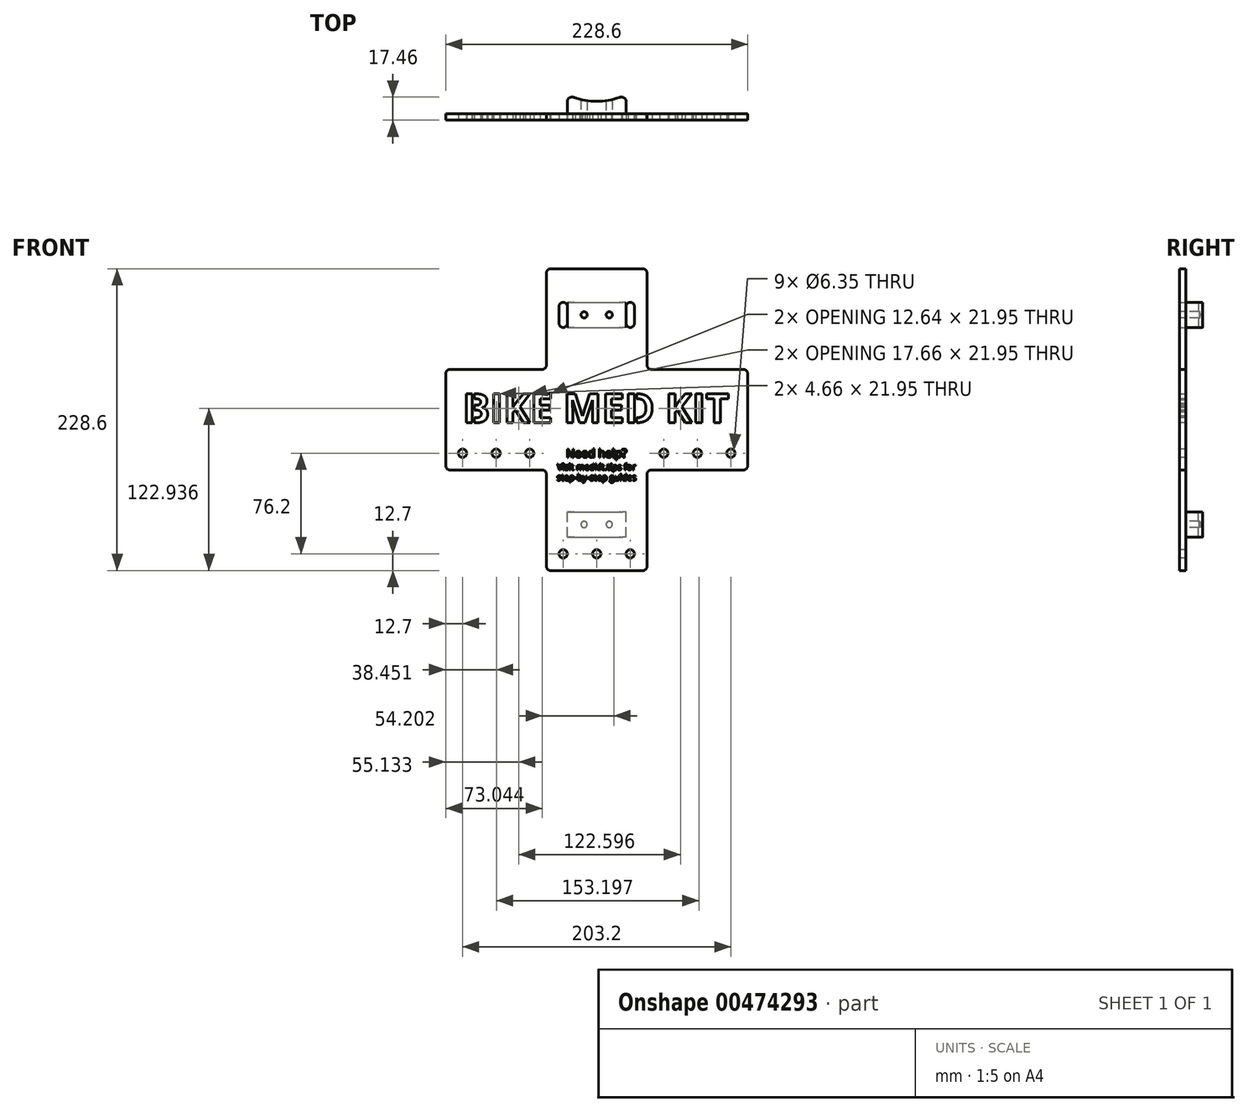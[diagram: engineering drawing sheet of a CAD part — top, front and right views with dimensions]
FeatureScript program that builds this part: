
annotation { "Feature Type Name" : "Feature", "Feature Type Description" : "" }
export const myFeature = defineFeature(function(context is Context, id is Id, definition is map)
    precondition{}
    {
        {
            var Q0;
            Q0=qCreatedBy(makeId("Front.planeOp"),FACE);
            var sketch = newSketch(context, id + "F0", { "sketchPlane" : qUnion([Q0])});
            skLineSegment(sketch, "E0.bottom", {"start": v(-38.1, 114.3) * mm, "end": v(38.1, 114.3) * mm});
            skLineSegment(sketch, "E0.top", {"start": v(-38.1, -114.3) * mm, "end": v(38.1, -114.3) * mm});
            skLineSegment(sketch, "E0.left", {"start": v(-38.1, 114.3) * mm, "end": v(-38.1, 38.1) * mm});
            skLineSegment(sketch, "E0.right", {"start": v(38.1, 114.3) * mm, "end": v(38.1, 38.1) * mm});
            skPoint(sketch, "E0.middle", {"position": v(0, 0) * mm});
            skLineSegment(sketch, "E1.bottom", {"start": v(114.3, 38.1) * mm, "end": v(38.1, 38.1) * mm});
            skLineSegment(sketch, "E1.top", {"start": v(114.3, -38.1) * mm, "end": v(38.1, -38.1) * mm});
            skLineSegment(sketch, "E1.left", {"start": v(114.3, 38.1) * mm, "end": v(114.3, -38.1) * mm});
            skLineSegment(sketch, "E1.right", {"start": v(-114.3, 38.1) * mm, "end": v(-114.3, -38.1) * mm});
            skLineSegment(sketch, "E2.trimOffspring", {"start": v(-38.1, 38.1) * mm, "end": v(-114.3, 38.1) * mm});
            skLineSegment(sketch, "E3.trimOffspring", {"start": v(-38.1, -38.1) * mm, "end": v(-38.1, -114.3) * mm});
            skLineSegment(sketch, "E4.trimOffspring", {"start": v(-38.1, -38.1) * mm, "end": v(-114.3, -38.1) * mm});
            skLineSegment(sketch, "E5.trimOffspring", {"start": v(38.1, -38.1) * mm, "end": v(38.1, -114.3) * mm});
            skSolve(sketch);
        }
        {
            var Q0;
            Q0 = qSketchRegion(id + "F0", true);
            extrude(context, id + "F1", {"entities" : qUnion([Q0]), "oppositeDirection" : true, "depth" : 4.76 * mm});
        }
        {
            var Q0;
            Q0=makeQuery(id+"F1.opExtrude","SWEPT_EDGE",EDGE,{"disambiguationData":[OSD([sQuery(id+"F0.wireOp",EDGE,"E0.right"),sQuery(id+"F0.wireOp",EDGE,"E1.bottom")])]});
            var Q1;
            Q1=makeQuery(id+"F1.opExtrude","SWEPT_EDGE",EDGE,{"disambiguationData":[OSD([sQuery(id+"F0.wireOp",EDGE,"E1.bottom"),sQuery(id+"F0.wireOp",EDGE,"E1.left")])]});
            var Q2;
            Q2=makeQuery(id+"F1.opExtrude","SWEPT_EDGE",EDGE,{"disambiguationData":[OSD([sQuery(id+"F0.wireOp",EDGE,"E1.top"),sQuery(id+"F0.wireOp",EDGE,"E1.left")])]});
            var Q3;
            Q3=makeQuery(id+"F1.opExtrude","SWEPT_EDGE",EDGE,{"disambiguationData":[OSD([sQuery(id+"F0.wireOp",EDGE,"E1.right"),sQuery(id+"F0.wireOp",EDGE,"E2.trimOffspring")])]});
            var Q4;
            Q4=makeQuery(id+"F1.opExtrude","SWEPT_EDGE",EDGE,{"disambiguationData":[OSD([sQuery(id+"F0.wireOp",EDGE,"E1.right"),sQuery(id+"F0.wireOp",EDGE,"E4.trimOffspring")])]});
            var Q5;
            Q5=makeQuery(id+"F1.opExtrude","SWEPT_EDGE",EDGE,{"disambiguationData":[OSD([sQuery(id+"F0.wireOp",EDGE,"E3.trimOffspring"),sQuery(id+"F0.wireOp",EDGE,"E4.trimOffspring")])]});
            var Q6;
            Q6=makeQuery(id+"F1.opExtrude","SWEPT_EDGE",EDGE,{"disambiguationData":[OSD([sQuery(id+"F0.wireOp",EDGE,"E1.top"),sQuery(id+"F0.wireOp",EDGE,"E5.trimOffspring")])]});
            var Q7;
            Q7=makeQuery(id+"F1.opExtrude","SWEPT_EDGE",EDGE,{"disambiguationData":[OSD([sQuery(id+"F0.wireOp",EDGE,"E0.left"),sQuery(id+"F0.wireOp",EDGE,"E2.trimOffspring")])]});
            var Q8;
            Q8=makeQuery(id+"F1.opExtrude","SWEPT_EDGE",EDGE,{"disambiguationData":[OSD([sQuery(id+"F0.wireOp",EDGE,"E0.bottom"),sQuery(id+"F0.wireOp",EDGE,"E0.right")])]});
            var Q9;
            Q9=makeQuery(id+"F1.opExtrude","SWEPT_EDGE",EDGE,{"disambiguationData":[OSD([sQuery(id+"F0.wireOp",EDGE,"E0.bottom"),sQuery(id+"F0.wireOp",EDGE,"E0.left")])]});
            var Q10;
            Q10=makeQuery(id+"F1.opExtrude","SWEPT_EDGE",EDGE,{"disambiguationData":[OSD([sQuery(id+"F0.wireOp",EDGE,"E0.top"),sQuery(id+"F0.wireOp",EDGE,"E5.trimOffspring")])]});
            var Q11;
            Q11=makeQuery(id+"F1.opExtrude","SWEPT_EDGE",EDGE,{"disambiguationData":[OSD([sQuery(id+"F0.wireOp",EDGE,"E0.top"),sQuery(id+"F0.wireOp",EDGE,"E3.trimOffspring")])]});
            fillet(context, id + "F2", {"entities" : qUnion([Q0, Q1, Q2, Q3, Q4, Q5, Q6, Q7, Q8, Q9, Q10, Q11]), "radius" : 3.17 * mm, "tangentPropagation" : true, "allowEdgeOverflow" : false});
        }
        {
            var Q0;
            Q0=makeQuery(id+"F1.opExtrude","CAP_FACE",FACE,{"disambiguationData":[OSD([sQuery(id+"F0.wireOp",EDGE,"E0.bottom"),sQuery(id+"F0.wireOp",EDGE,"E0.top"),sQuery(id+"F0.wireOp",EDGE,"E0.left"),sQuery(id+"F0.wireOp",EDGE,"E0.right"),sQuery(id+"F0.wireOp",EDGE,"E1.bottom"),sQuery(id+"F0.wireOp",EDGE,"E1.top"),sQuery(id+"F0.wireOp",EDGE,"E1.left"),sQuery(id+"F0.wireOp",EDGE,"E1.right"),sQuery(id+"F0.wireOp",EDGE,"E2.trimOffspring"),sQuery(id+"F0.wireOp",EDGE,"E3.trimOffspring"),sQuery(id+"F0.wireOp",EDGE,"E4.trimOffspring"),sQuery(id+"F0.wireOp",EDGE,"E5.trimOffspring")])],"isStart":true});
            var sketch = newSketch(context, id + "F3", { "sketchPlane" : qUnion([Q0])});
            skCircle(sketch, "E6", {"center": v(-101.6, -25.4) * mm, "radius": 3.18 * mm});
            skCircle(sketch, "E7.1.0.0", {"center": v(-76.2, -25.4) * mm, "radius": 3.18 * mm});
            skCircle(sketch, "E7.2.0.0", {"center": v(-50.8, -25.4) * mm, "radius": 3.18 * mm});
            skLineSegment(sketch, "E7.direction1", {"start": v(-101.6, -25.4) * mm, "end": v(-76.2, -25.4) * mm, "construction": true});
            skCircle(sketch, "E8", {"center": v(-25.4, -101.6) * mm, "radius": 3.18 * mm});
            skCircle(sketch, "E9", {"center": v(101.6, -25.4) * mm, "radius": 3.18 * mm});
            skCircle(sketch, "E10.1.0.0", {"center": v(76.2, -25.4) * mm, "radius": 3.18 * mm});
            skCircle(sketch, "E10.2.0.0", {"center": v(50.8, -25.4) * mm, "radius": 3.18 * mm});
            skLineSegment(sketch, "E10.direction1", {"start": v(101.6, -25.4) * mm, "end": v(76.2, -25.4) * mm, "construction": true});
            skCircle(sketch, "E11.1.0.0", {"center": v(0, -101.6) * mm, "radius": 3.18 * mm});
            skCircle(sketch, "E11.2.0.0", {"center": v(25.4, -101.6) * mm, "radius": 3.18 * mm});
            skLineSegment(sketch, "E11.direction1", {"start": v(-25.4, -101.6) * mm, "end": v(0, -101.6) * mm, "construction": true});
            skSolve(sketch);
        }
        {
            var Q0;
            Q0 = qSketchRegion(id + "F3", true);
            extrude(context, id + "F4", {"entities" : qUnion([Q0]), "operationType" : NewBodyOperationType.REMOVE, "endBound" : BoundingType.THROUGH_ALL, "oppositeDirection" : true, "depth" : 25.4 * mm});
        }
        {
            var Q0;
            Q0=makeQuery(id+"F1.opExtrude","CAP_FACE",FACE,{"disambiguationData":[OSD([sQuery(id+"F0.wireOp",EDGE,"E0.bottom"),sQuery(id+"F0.wireOp",EDGE,"E0.top"),sQuery(id+"F0.wireOp",EDGE,"E0.left"),sQuery(id+"F0.wireOp",EDGE,"E0.right"),sQuery(id+"F0.wireOp",EDGE,"E1.bottom"),sQuery(id+"F0.wireOp",EDGE,"E1.top"),sQuery(id+"F0.wireOp",EDGE,"E1.left"),sQuery(id+"F0.wireOp",EDGE,"E1.right"),sQuery(id+"F0.wireOp",EDGE,"E2.trimOffspring"),sQuery(id+"F0.wireOp",EDGE,"E3.trimOffspring"),sQuery(id+"F0.wireOp",EDGE,"E4.trimOffspring"),sQuery(id+"F0.wireOp",EDGE,"E5.trimOffspring")])],"isStart":true});
            var sketch = newSketch(context, id + "F5", { "sketchPlane" : qUnion([Q0])});
            skText(sketch, "E12", { "text": "BIKE MED KIT", "fontName": "OpenSans-Bold.ttf"});
            skLineSegment(sketch, "E13", {"start": v(-101.6, -22.23) * mm, "end": v(-50.8, -22.22) * mm, "construction": true});
            skLineSegment(sketch, "E14", {"start": v(-101.6, 7.94) * mm, "end": v(101.6, 7.94) * mm, "construction": true});
            const initialGuessF5  = {"E12": [-0.1016, -0.00234, 1, 0, 0.02214]};
            skSetInitialGuess(sketch, initialGuessF5);
            skSolve(sketch);
        }
        {
            var Q0;
            Q0 = qSketchRegion(id + "F5", true);
            extrude(context, id + "F6", {"entities" : qUnion([Q0]), "operationType" : NewBodyOperationType.REMOVE, "endBound" : BoundingType.THROUGH_ALL, "oppositeDirection" : true, "depth" : 25.4 * mm});
        }
        {
            var Q0;
            {var subQ0=sQuery(id+"F0.wireOp",EDGE,"E2.trimOffspring");var subQ1=sQuery(id+"F0.wireOp",EDGE,"E1.right");var subQ2=sQuery(id+"F0.wireOp",EDGE,"E5.trimOffspring");var subQ3=sQuery(id+"F0.wireOp",EDGE,"E1.top");var subQ4=sQuery(id+"F0.wireOp",EDGE,"E1.left");var subQ5=sQuery(id+"F0.wireOp",EDGE,"E0.left");var subQ6=sQuery(id+"F0.wireOp",EDGE,"E1.bottom");var subQ7=sQuery(id+"F0.wireOp",EDGE,"E4.trimOffspring");var subQ8=sQuery(id+"F0.wireOp",EDGE,"E0.top");var subQ9=sQuery(id+"F0.wireOp",EDGE,"E0.right");var subQ10=sQuery(id+"F0.wireOp",EDGE,"E0.bottom");var subQ11=sQuery(id+"F0.wireOp",EDGE,"E3.trimOffspring");Q0=makeQuery(id+"F6.boolean.opBoolean","SPLIT",FACE,{"disambiguationData":[TD([makeQuery(id+"F1.opExtrude","SWEPT_FACE",FACE,{"disambiguationData":[OSD([subQ10])]})])],"derivedFrom":makeQuery(id+"F1.opExtrude","CAP_FACE",FACE,{"disambiguationData":[OSD([subQ10,subQ8,subQ5,subQ9,subQ6,subQ3,subQ4,subQ1,subQ0,subQ11,subQ7,subQ2])],"isStart":true})});}
            var sketch = newSketch(context, id + "F7", { "sketchPlane" : qUnion([Q0])});
            skLineSegment(sketch, "E15.bottom", {"start": v(-94.18, 23) * mm, "end": v(-92.6, 23) * mm});
            skLineSegment(sketch, "E15.top", {"start": v(-94.18, -7.38) * mm, "end": v(-92.6, -7.38) * mm});
            skLineSegment(sketch, "E15.left", {"start": v(-94.18, 23) * mm, "end": v(-94.18, -7.38) * mm});
            skLineSegment(sketch, "E15.right", {"start": v(-92.6, 23) * mm, "end": v(-92.6, -7.38) * mm});
            skLineSegment(sketch, "E16.bottom", {"start": v(28.49, 25.23) * mm, "end": v(30.07, 25.23) * mm});
            skLineSegment(sketch, "E16.top", {"start": v(28.49, -11.56) * mm, "end": v(30.07, -11.56) * mm});
            skLineSegment(sketch, "E16.left", {"start": v(28.49, 25.23) * mm, "end": v(28.49, -11.56) * mm});
            skLineSegment(sketch, "E16.right", {"start": v(30.07, 25.23) * mm, "end": v(30.07, -11.56) * mm});
            skSolve(sketch);
        }
        {
            var Q0;
            Q0 = qSketchRegion(id + "F7", true);
            var Q1;
            {var subQ0=sQuery(id+"F0.wireOp",EDGE,"E2.trimOffspring");var subQ1=sQuery(id+"F0.wireOp",EDGE,"E1.right");var subQ2=sQuery(id+"F0.wireOp",EDGE,"E5.trimOffspring");var subQ3=sQuery(id+"F0.wireOp",EDGE,"E1.top");var subQ4=sQuery(id+"F0.wireOp",EDGE,"E1.left");var subQ5=sQuery(id+"F0.wireOp",EDGE,"E0.left");var subQ6=sQuery(id+"F0.wireOp",EDGE,"E1.bottom");var subQ7=sQuery(id+"F0.wireOp",EDGE,"E4.trimOffspring");var subQ8=sQuery(id+"F0.wireOp",EDGE,"E0.top");var subQ9=sQuery(id+"F0.wireOp",EDGE,"E0.right");var subQ10=sQuery(id+"F0.wireOp",EDGE,"E0.bottom");var subQ11=sQuery(id+"F0.wireOp",EDGE,"E3.trimOffspring");Q1=makeQuery(id+"F6.boolean.opBoolean","SPLIT",FACE,{"disambiguationData":[TD([makeQuery(id+"F1.opExtrude","SWEPT_FACE",FACE,{"disambiguationData":[OSD([subQ10])]})])],"derivedFrom":makeQuery(id+"F1.opExtrude","CAP_FACE",FACE,{"disambiguationData":[OSD([subQ10,subQ8,subQ5,subQ9,subQ6,subQ3,subQ4,subQ1,subQ0,subQ11,subQ7,subQ2])],"isStart":false})});}
            extrude(context, id + "F8", {"entities" : qUnion([Q0]), "operationType" : NewBodyOperationType.ADD, "endBound" : BoundingType.UP_TO_SURFACE, "oppositeDirection" : true, "endBoundEntityFace" : qUnion([Q1]), "depth" : 25.4 * mm});
        }
        {
            var Q0;
            {var subQ0=sQuery(id+"F0.wireOp",EDGE,"E5.trimOffspring");var subQ1=sQuery(id+"F0.wireOp",EDGE,"E4.trimOffspring");var subQ2=sQuery(id+"F0.wireOp",EDGE,"E3.trimOffspring");var subQ3=sQuery(id+"F0.wireOp",EDGE,"E2.trimOffspring");var subQ4=sQuery(id+"F0.wireOp",EDGE,"E1.right");var subQ5=sQuery(id+"F0.wireOp",EDGE,"E1.left");var subQ6=sQuery(id+"F0.wireOp",EDGE,"E1.top");var subQ7=sQuery(id+"F0.wireOp",EDGE,"E1.bottom");var subQ8=sQuery(id+"F0.wireOp",EDGE,"E0.right");var subQ9=sQuery(id+"F0.wireOp",EDGE,"E0.left");var subQ10=sQuery(id+"F0.wireOp",EDGE,"E0.top");var subQ11=sQuery(id+"F0.wireOp",EDGE,"E0.bottom");var subQ12=makeQuery(id+"F1.opExtrude","CAP_FACE",FACE,{"disambiguationData":[OSD([subQ11,subQ10,subQ9,subQ8,subQ7,subQ6,subQ5,subQ4,subQ3,subQ2,subQ1,subQ0])],"isStart":true});Q0=makeQuery(id+"F8.boolean.opBoolean","MERGE",FACE,{"derivedFrom":[makeQuery(id+"F6.boolean.opBoolean","SPLIT",FACE,{"disambiguationData":[TD([makeQuery(id+"F1.opExtrude","SWEPT_FACE",FACE,{"disambiguationData":[OSD([subQ11])]})])],"derivedFrom":subQ12}),makeQuery(id+"F6.boolean.opBoolean","SPLIT",FACE,{"disambiguationData":[TD([makeQuery(id+"F6.opExtrude","SWEPT_FACE",FACE,{"disambiguationData":[OSD([sQuery(id+"F5.wireOp",EDGE,"E12.sketch_text.stroke-12")])]})])],"derivedFrom":subQ12}),makeQuery(id+"F6.boolean.opBoolean","SPLIT",FACE,{"disambiguationData":[TD([makeQuery(id+"F6.opExtrude","SWEPT_FACE",FACE,{"disambiguationData":[OSD([sQuery(id+"F5.wireOp",EDGE,"E12.sketch_text.stroke-19")])]})])],"derivedFrom":subQ12}),makeQuery(id+"F6.boolean.opBoolean","SPLIT",FACE,{"disambiguationData":[TD([makeQuery(id+"F6.opExtrude","SWEPT_FACE",FACE,{"disambiguationData":[OSD([sQuery(id+"F5.wireOp",EDGE,"E12.sketch_text.stroke-92")])]})])],"derivedFrom":subQ12}),makeQuery(id+"F8.opExtrude","CAP_FACE",FACE,{"disambiguationData":[OSD([sQuery(id+"F7.wireOp",EDGE,"E15.bottom"),sQuery(id+"F7.wireOp",EDGE,"E15.top"),sQuery(id+"F7.wireOp",EDGE,"E15.left"),sQuery(id+"F7.wireOp",EDGE,"E15.right")])],"isStart":true}),makeQuery(id+"F8.opExtrude","CAP_FACE",FACE,{"disambiguationData":[OSD([sQuery(id+"F7.wireOp",EDGE,"E16.bottom"),sQuery(id+"F7.wireOp",EDGE,"E16.top"),sQuery(id+"F7.wireOp",EDGE,"E16.left"),sQuery(id+"F7.wireOp",EDGE,"E16.right")])],"isStart":true})]});}
            var sketch = newSketch(context, id + "F9", { "sketchPlane" : qUnion([Q0])});
            skLineSegment(sketch, "E17.bottom", {"start": v(-28.57, 88.9) * mm, "end": v(-22.22, 88.9) * mm});
            skLineSegment(sketch, "E17.top", {"start": v(-28.57, 69.85) * mm, "end": v(-22.22, 69.85) * mm});
            skLineSegment(sketch, "E17.left", {"start": v(-28.57, 88.9) * mm, "end": v(-28.57, 69.85) * mm});
            skLineSegment(sketch, "E17.right", {"start": v(-22.22, 88.9) * mm, "end": v(-22.22, 69.85) * mm});
            skLineSegment(sketch, "E18.MirrorCS", {"start": v(22.22, 88.9) * mm, "end": v(22.22, 69.85) * mm});
            skLineSegment(sketch, "E19.MirrorCS", {"start": v(28.57, 69.85) * mm, "end": v(22.22, 69.85) * mm});
            skLineSegment(sketch, "E20.MirrorCS", {"start": v(28.57, 88.9) * mm, "end": v(28.57, 69.85) * mm});
            skLineSegment(sketch, "E21.MirrorCS", {"start": v(28.57, 88.9) * mm, "end": v(22.22, 88.9) * mm});
            skSolve(sketch);
        }
        {
            var Q0;
            Q0 = qSketchRegion(id + "F9", true);
            extrude(context, id + "F10", {"entities" : qUnion([Q0]), "operationType" : NewBodyOperationType.REMOVE, "endBound" : BoundingType.THROUGH_ALL, "oppositeDirection" : true, "depth" : 25.4 * mm});
        }
        {
            var Q0;
            Q0=makeQuery(id+"F10.boolean.opBoolean","COPY",EDGE,{"derivedFrom":makeQuery(id+"F10.opExtrude","SWEPT_EDGE",EDGE,{"disambiguationData":[OSD([sQuery(id+"F9.wireOp",EDGE,"E17.top"),sQuery(id+"F9.wireOp",EDGE,"E17.left")])]})});
            var Q1;
            Q1=makeQuery(id+"F10.boolean.opBoolean","COPY",EDGE,{"derivedFrom":makeQuery(id+"F10.opExtrude","SWEPT_EDGE",EDGE,{"disambiguationData":[OSD([sQuery(id+"F9.wireOp",EDGE,"E17.top"),sQuery(id+"F9.wireOp",EDGE,"E17.right")])]})});
            var Q2;
            Q2=makeQuery(id+"F10.boolean.opBoolean","COPY",EDGE,{"derivedFrom":makeQuery(id+"F10.opExtrude","SWEPT_EDGE",EDGE,{"disambiguationData":[OSD([sQuery(id+"F9.wireOp",EDGE,"E19.MirrorCS"),sQuery(id+"F9.wireOp",EDGE,"E20.MirrorCS")])]})});
            var Q3;
            Q3=makeQuery(id+"F10.boolean.opBoolean","COPY",EDGE,{"derivedFrom":makeQuery(id+"F10.opExtrude","SWEPT_EDGE",EDGE,{"disambiguationData":[OSD([sQuery(id+"F9.wireOp",EDGE,"E18.MirrorCS"),sQuery(id+"F9.wireOp",EDGE,"E19.MirrorCS")])]})});
            var Q4;
            Q4=makeQuery(id+"F10.boolean.opBoolean","COPY",EDGE,{"derivedFrom":makeQuery(id+"F10.opExtrude","SWEPT_EDGE",EDGE,{"disambiguationData":[OSD([sQuery(id+"F9.wireOp",EDGE,"E18.MirrorCS"),sQuery(id+"F9.wireOp",EDGE,"E21.MirrorCS")])]})});
            var Q5;
            Q5=makeQuery(id+"F10.boolean.opBoolean","COPY",EDGE,{"derivedFrom":makeQuery(id+"F10.opExtrude","SWEPT_EDGE",EDGE,{"disambiguationData":[OSD([sQuery(id+"F9.wireOp",EDGE,"E17.bottom"),sQuery(id+"F9.wireOp",EDGE,"E17.left")])]})});
            var Q6;
            Q6=makeQuery(id+"F10.boolean.opBoolean","COPY",EDGE,{"derivedFrom":makeQuery(id+"F10.opExtrude","SWEPT_EDGE",EDGE,{"disambiguationData":[OSD([sQuery(id+"F9.wireOp",EDGE,"E17.bottom"),sQuery(id+"F9.wireOp",EDGE,"E17.right")])]})});
            var Q7;
            Q7=makeQuery(id+"F10.boolean.opBoolean","COPY",EDGE,{"derivedFrom":makeQuery(id+"F10.opExtrude","SWEPT_EDGE",EDGE,{"disambiguationData":[OSD([sQuery(id+"F9.wireOp",EDGE,"E20.MirrorCS"),sQuery(id+"F9.wireOp",EDGE,"E21.MirrorCS")])]})});
            fillet(context, id + "F11", {"entities" : qUnion([Q0, Q1, Q2, Q3, Q4, Q5, Q6, Q7]), "radius" : 3.17 * mm, "tangentPropagation" : true, "allowEdgeOverflow" : false});
        }
        {
            var Q0;
            {var subQ0=sQuery(id+"F0.wireOp",EDGE,"E5.trimOffspring");var subQ1=sQuery(id+"F0.wireOp",EDGE,"E4.trimOffspring");var subQ2=sQuery(id+"F0.wireOp",EDGE,"E3.trimOffspring");var subQ3=sQuery(id+"F0.wireOp",EDGE,"E2.trimOffspring");var subQ4=sQuery(id+"F0.wireOp",EDGE,"E1.right");var subQ5=sQuery(id+"F0.wireOp",EDGE,"E1.left");var subQ6=sQuery(id+"F0.wireOp",EDGE,"E1.top");var subQ7=sQuery(id+"F0.wireOp",EDGE,"E1.bottom");var subQ8=sQuery(id+"F0.wireOp",EDGE,"E0.right");var subQ9=sQuery(id+"F0.wireOp",EDGE,"E0.left");var subQ10=sQuery(id+"F0.wireOp",EDGE,"E0.top");var subQ11=sQuery(id+"F0.wireOp",EDGE,"E0.bottom");var subQ12=makeQuery(id+"F1.opExtrude","CAP_FACE",FACE,{"disambiguationData":[OSD([subQ11,subQ10,subQ9,subQ8,subQ7,subQ6,subQ5,subQ4,subQ3,subQ2,subQ1,subQ0])],"isStart":true});Q0=makeQuery(id+"F8.boolean.opBoolean","MERGE",FACE,{"derivedFrom":[makeQuery(id+"F6.boolean.opBoolean","SPLIT",FACE,{"disambiguationData":[TD([makeQuery(id+"F1.opExtrude","SWEPT_FACE",FACE,{"disambiguationData":[OSD([subQ11])]})])],"derivedFrom":subQ12}),makeQuery(id+"F6.boolean.opBoolean","SPLIT",FACE,{"disambiguationData":[TD([makeQuery(id+"F6.opExtrude","SWEPT_FACE",FACE,{"disambiguationData":[OSD([sQuery(id+"F5.wireOp",EDGE,"E12.sketch_text.stroke-12")])]})])],"derivedFrom":subQ12}),makeQuery(id+"F6.boolean.opBoolean","SPLIT",FACE,{"disambiguationData":[TD([makeQuery(id+"F6.opExtrude","SWEPT_FACE",FACE,{"disambiguationData":[OSD([sQuery(id+"F5.wireOp",EDGE,"E12.sketch_text.stroke-19")])]})])],"derivedFrom":subQ12}),makeQuery(id+"F6.boolean.opBoolean","SPLIT",FACE,{"disambiguationData":[TD([makeQuery(id+"F6.opExtrude","SWEPT_FACE",FACE,{"disambiguationData":[OSD([sQuery(id+"F5.wireOp",EDGE,"E12.sketch_text.stroke-92")])]})])],"derivedFrom":subQ12}),makeQuery(id+"F8.opExtrude","CAP_FACE",FACE,{"disambiguationData":[OSD([sQuery(id+"F7.wireOp",EDGE,"E15.bottom"),sQuery(id+"F7.wireOp",EDGE,"E15.top"),sQuery(id+"F7.wireOp",EDGE,"E15.left"),sQuery(id+"F7.wireOp",EDGE,"E15.right")])],"isStart":true}),makeQuery(id+"F8.opExtrude","CAP_FACE",FACE,{"disambiguationData":[OSD([sQuery(id+"F7.wireOp",EDGE,"E16.bottom"),sQuery(id+"F7.wireOp",EDGE,"E16.top"),sQuery(id+"F7.wireOp",EDGE,"E16.left"),sQuery(id+"F7.wireOp",EDGE,"E16.right")])],"isStart":true})]});}
            var sketch = newSketch(context, id + "F12", { "sketchPlane" : qUnion([Q0])});
            skCircle(sketch, "E22", {"center": v(-9.53, 79.38) * mm, "radius": 2.38 * mm});
            skCircle(sketch, "E23", {"center": v(9.53, 79.38) * mm, "radius": 2.38 * mm});
            skLineSegment(sketch, "E24", {"start": v(-22.22, 79.38) * mm, "end": v(22.22, 79.38) * mm, "construction": true});
            skSolve(sketch);
        }
        {
            var Q0;
            Q0 = qSketchRegion(id + "F12", true);
            extrude(context, id + "F13", {"entities" : qUnion([Q0]), "operationType" : NewBodyOperationType.REMOVE, "endBound" : BoundingType.THROUGH_ALL, "oppositeDirection" : true, "depth" : 25.4 * mm});
        }
        {
            var Q0;
            Q0=qCreatedBy(makeId("Top.planeOp"),FACE);
            cPlane(context, id + "F14", {"entities" : qUnion([Q0]), "cplaneType" : CPlaneType.OFFSET, "offset" : 79.38 * mm, "width" : 152.4 * mm, "height" : 152.4 * mm});
        }
        {
            var Q0;
            Q0=qCreatedBy(id+"F14.planeOp",FACE);
            var sketch = newSketch(context, id + "F15", { "sketchPlane" : qUnion([Q0])});
            skLineSegment(sketch, "E25.bottom", {"start": v(-22.22, 4.76) * mm, "end": v(22.23, 4.76) * mm});
            skLineSegment(sketch, "E25.top", {"start": v(-22.22, 17.46) * mm, "end": v(-17.68, 17.46) * mm});
            skLineSegment(sketch, "E25.left", {"start": v(-22.22, 4.76) * mm, "end": v(-22.22, 17.46) * mm});
            skLineSegment(sketch, "E25.right", {"start": v(22.23, 4.76) * mm, "end": v(22.23, 17.46) * mm});
            skArc(sketch, "E26", {"start": v(-17.68, 17.46) * mm, "mid": v(0, 14.29) * mm, "end": v(17.68, 17.46) * mm});
            skLineSegment(sketch, "E27", {"start": v(0, 17.46) * mm, "end": v(0, 65.09) * mm, "construction": true});
            skPoint(sketch, "E27.endSnap0", {"position": v(0, 17.46) * mm});
            skLineSegment(sketch, "E28.trimOffspring", {"start": v(17.68, 17.46) * mm, "end": v(22.23, 17.46) * mm});
            skSolve(sketch);
        }
        {
            var Q0;
            Q0 = qSketchRegion(id + "F15", true);
            extrude(context, id + "F16", {"entities" : qUnion([Q0]), "depth" : 9.52 * mm, "hasSecondDirection" : true, "secondDirectionOppositeDirection" : true, "secondDirectionDepth" : 9.52 * mm});
        }
        {
            var Q0;
            Q0=makeQuery(id+"F16.opExtrude","SWEPT_EDGE",EDGE,{"disambiguationData":[OSD([sQuery(id+"F15.wireOp",EDGE,"E26"),sQuery(id+"F15.wireOp",EDGE,"E28.trimOffspring")])]});
            var Q1;
            Q1=makeQuery(id+"F16.opExtrude","SWEPT_EDGE",EDGE,{"disambiguationData":[OSD([sQuery(id+"F15.wireOp",EDGE,"E25.right"),sQuery(id+"F15.wireOp",EDGE,"E28.trimOffspring")])]});
            var Q2;
            Q2=makeQuery(id+"F16.opExtrude","SWEPT_EDGE",EDGE,{"disambiguationData":[OSD([sQuery(id+"F15.wireOp",EDGE,"E25.top"),sQuery(id+"F15.wireOp",EDGE,"E26")])]});
            var Q3;
            Q3=makeQuery(id+"F16.opExtrude","SWEPT_EDGE",EDGE,{"disambiguationData":[OSD([sQuery(id+"F15.wireOp",EDGE,"E25.top"),sQuery(id+"F15.wireOp",EDGE,"E25.left")])]});
            fillet(context, id + "F17", {"entities" : qUnion([Q0, Q1, Q2, Q3]), "radius" : 3.17 * mm, "tangentPropagation" : true, "allowEdgeOverflow" : false});
        }
        {
            var Q0;
            Q0 = qSketchRegion(id + "F12", true);
            extrude(context, id + "F18", {"entities" : qUnion([Q0]), "operationType" : NewBodyOperationType.REMOVE, "endBound" : BoundingType.THROUGH_ALL, "oppositeDirection" : true, "depth" : 25.4 * mm});
        }
        {
            var Q0;
            Q0=makeQuery(id+"F16.opExtrude","SWEPT_BODY",BODY,{"disambiguationData":[OSD([sQuery(id+"F15.wireOp",EDGE,"E25.bottom"),sQuery(id+"F15.wireOp",EDGE,"E25.top"),sQuery(id+"F15.wireOp",EDGE,"E25.left"),sQuery(id+"F15.wireOp",EDGE,"E25.right"),sQuery(id+"F15.wireOp",EDGE,"E26"),sQuery(id+"F15.wireOp",EDGE,"E28.trimOffspring")])]});
            var Q1;
            Q1=qCreatedBy(makeId("Top.planeOp"),FACE);
            mirror(context, id + "F19", {"entities" : qUnion([Q0]), "mirrorPlane" : qUnion([Q1])});
        }
        {
            var Q0;
            {var subQ0=sQuery(id+"F0.wireOp",EDGE,"E5.trimOffspring");var subQ1=sQuery(id+"F0.wireOp",EDGE,"E4.trimOffspring");var subQ2=sQuery(id+"F0.wireOp",EDGE,"E3.trimOffspring");var subQ3=sQuery(id+"F0.wireOp",EDGE,"E2.trimOffspring");var subQ4=sQuery(id+"F0.wireOp",EDGE,"E1.right");var subQ5=sQuery(id+"F0.wireOp",EDGE,"E1.left");var subQ6=sQuery(id+"F0.wireOp",EDGE,"E1.top");var subQ7=sQuery(id+"F0.wireOp",EDGE,"E1.bottom");var subQ8=sQuery(id+"F0.wireOp",EDGE,"E0.right");var subQ9=sQuery(id+"F0.wireOp",EDGE,"E0.left");var subQ10=sQuery(id+"F0.wireOp",EDGE,"E0.top");var subQ11=sQuery(id+"F0.wireOp",EDGE,"E0.bottom");var subQ12=makeQuery(id+"F1.opExtrude","CAP_FACE",FACE,{"disambiguationData":[OSD([subQ11,subQ10,subQ9,subQ8,subQ7,subQ6,subQ5,subQ4,subQ3,subQ2,subQ1,subQ0])],"isStart":true});Q0=makeQuery(id+"F8.boolean.opBoolean","MERGE",FACE,{"derivedFrom":[makeQuery(id+"F6.boolean.opBoolean","SPLIT",FACE,{"disambiguationData":[TD([makeQuery(id+"F1.opExtrude","SWEPT_FACE",FACE,{"disambiguationData":[OSD([subQ11])]})])],"derivedFrom":subQ12}),makeQuery(id+"F6.boolean.opBoolean","SPLIT",FACE,{"disambiguationData":[TD([makeQuery(id+"F6.opExtrude","SWEPT_FACE",FACE,{"disambiguationData":[OSD([sQuery(id+"F5.wireOp",EDGE,"E12.sketch_text.stroke-12")])]})])],"derivedFrom":subQ12}),makeQuery(id+"F6.boolean.opBoolean","SPLIT",FACE,{"disambiguationData":[TD([makeQuery(id+"F6.opExtrude","SWEPT_FACE",FACE,{"disambiguationData":[OSD([sQuery(id+"F5.wireOp",EDGE,"E12.sketch_text.stroke-19")])]})])],"derivedFrom":subQ12}),makeQuery(id+"F6.boolean.opBoolean","SPLIT",FACE,{"disambiguationData":[TD([makeQuery(id+"F6.opExtrude","SWEPT_FACE",FACE,{"disambiguationData":[OSD([sQuery(id+"F5.wireOp",EDGE,"E12.sketch_text.stroke-92")])]})])],"derivedFrom":subQ12}),makeQuery(id+"F8.opExtrude","CAP_FACE",FACE,{"disambiguationData":[OSD([sQuery(id+"F7.wireOp",EDGE,"E15.bottom"),sQuery(id+"F7.wireOp",EDGE,"E15.top"),sQuery(id+"F7.wireOp",EDGE,"E15.left"),sQuery(id+"F7.wireOp",EDGE,"E15.right")])],"isStart":true}),makeQuery(id+"F8.opExtrude","CAP_FACE",FACE,{"disambiguationData":[OSD([sQuery(id+"F7.wireOp",EDGE,"E16.bottom"),sQuery(id+"F7.wireOp",EDGE,"E16.top"),sQuery(id+"F7.wireOp",EDGE,"E16.left"),sQuery(id+"F7.wireOp",EDGE,"E16.right")])],"isStart":true})]});}
            var sketch = newSketch(context, id + "F20", { "sketchPlane" : qUnion([Q0])});
            skText(sketch, "E29", { "text": "Need help?", "fontName": "OpenSans-Regular.ttf"});
            skText(sketch, "E30", { "text": "Visit medkit.tips for", "fontName": "OpenSans-Regular.ttf"});
            skText(sketch, "E31", { "text": "step-by-step guides", "fontName": "OpenSans-Regular.ttf"});
            const initialGuessF20  = {"E29": [-0.02318, -0.02858, 1, 0, 0.00635], "E30": [-0.02993, -0.0381, 1, 0, 0.00476], "E31": [-0.03014, -0.04604, 1, 0, 0.00476]};
            skSetInitialGuess(sketch, initialGuessF20);
            skSolve(sketch);
        }
        {
            var Q0;
            Q0 = qSketchRegion(id + "F20", true);
            var Q1;
            Q1 = qConstructionFilter(qBodyType(qCreatedBy(id + "F20" ,EDGE), BodyType.WIRE), ConstructionObject.NO);
            extrude(context, id + "F21", {"entities" : qUnion([Q0]), "operationType" : NewBodyOperationType.REMOVE, "surfaceEntities" : qUnion([Q1]), "oppositeDirection" : true, "depth" : 0.03 * mm});
        }
    });
